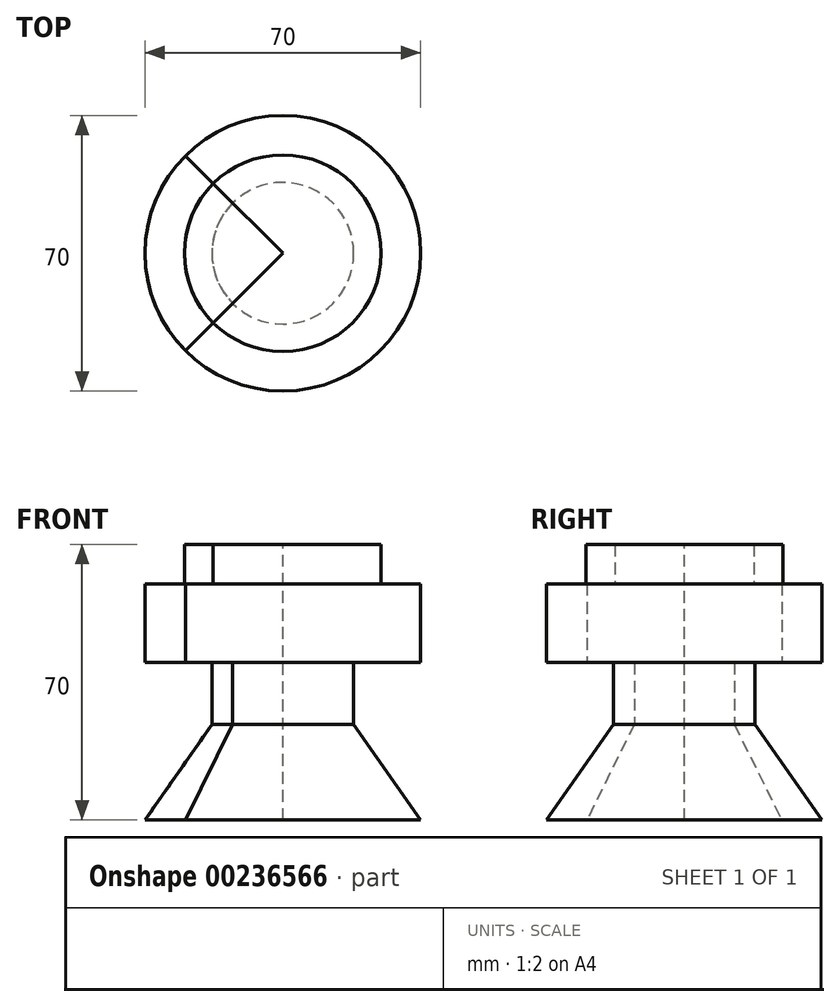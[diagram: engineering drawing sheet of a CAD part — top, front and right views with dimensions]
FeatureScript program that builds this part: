
annotation { "Feature Type Name" : "Feature", "Feature Type Description" : "" }
export const myFeature = defineFeature(function(context is Context, id is Id, definition is map)
    precondition{}
    {
        {
            var Q0;
            Q0=qCreatedBy(makeId("Front.planeOp"),FACE);
            var sketch = newSketch(context, id + "F0", { "sketchPlane" : qUnion([Q0])});
            skLineSegment(sketch, "E0", {"start": v(-25, 40) * mm, "end": v(-25, 30) * mm});
            skLineSegment(sketch, "E1", {"start": v(-25, 30) * mm, "end": v(-35, 30) * mm});
            skLineSegment(sketch, "E2", {"start": v(-35, 30) * mm, "end": v(-35, 10) * mm});
            skLineSegment(sketch, "E3", {"start": v(-35, 10) * mm, "end": v(-18, 10) * mm});
            skLineSegment(sketch, "E4", {"start": v(-18, 10) * mm, "end": v(-18, -5.72) * mm});
            skLineSegment(sketch, "E5", {"start": v(-18, -5.72) * mm, "end": v(-35, -30) * mm});
            skLineSegment(sketch, "E6", {"start": v(-35, -30) * mm, "end": v(0, -30) * mm});
            skLineSegment(sketch, "E7", {"start": v(0, -30) * mm, "end": v(0, 40) * mm});
            skLineSegment(sketch, "E8", {"start": v(0, 40) * mm, "end": v(-25, 40) * mm});
            skSolve(sketch);
        }
        {
            var Q0;
            Q0=makeQuery(id+"F0.imprint","IMPRINT",FACE,{"disambiguationData":[TD([[makeQuery(id+"F0.imprint","IMPRINT",EDGE,{"derivedFrom":sQuery(id+"F0.wireOp",EDGE,"E0")}),1.0]])]});
            var Q1;
            Q1=sQuery(id+"F0.wireOp",EDGE,"E7");
            revolve(context, id + "F1", {"entities" : qUnion([Q0]), "axis" : qUnion([Q1]), "revolveType" : RevolveType.SYMMETRIC, "angle" : 90 * degree});
        }
        {
            var Q0;
            Q0 = qSketchRegion(id + "F0", true);
            var Q1;
            Q1=sQuery(id+"F0.wireOp",EDGE,"E7");
            revolve(context, id + "F2", {"entities" : qUnion([Q0]), "axis" : qUnion([Q1]), "revolveType" : RevolveType.ONE_DIRECTION, "angle" : 360 * degree});
        }
    });
